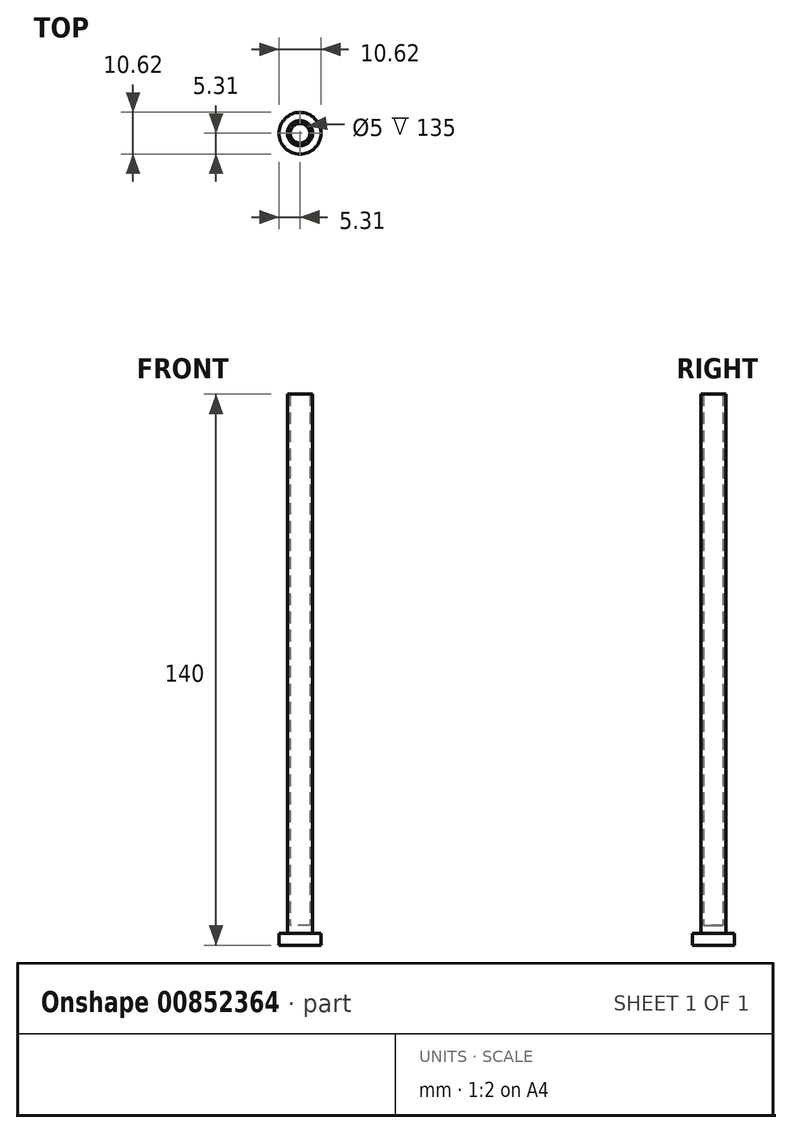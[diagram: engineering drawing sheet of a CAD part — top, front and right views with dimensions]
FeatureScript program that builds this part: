
annotation { "Feature Type Name" : "Feature", "Feature Type Description" : "" }
export const myFeature = defineFeature(function(context is Context, id is Id, definition is map)
    precondition{}
    {
        {
            var Q0;
            Q0=qCreatedBy(makeId("Top.planeOp"),FACE);
            var sketch = newSketch(context, id + "F0", { "sketchPlane" : qUnion([Q0])});
            skCircle(sketch, "E0", {"center": v(0, 0) * mm, "radius": 2.5 * mm});
            skCircle(sketch, "E1.0", {"center": v(0, 0) * mm, "radius": 3.2 * mm});
            skCircle(sketch, "E2", {"center": v(0, 0) * mm, "radius": 5.3 * mm});
            skSolve(sketch);
        }
        {
            var Q0;
            Q0 = qSketchRegion(id + "F0", true);
            var Q1;
            Q1=makeQuery(id+"F0.imprint","IMPRINT",FACE,{"disambiguationData":[TD([[makeQuery(id+"F0.imprint","IMPRINT",EDGE,{"derivedFrom":sQuery(id+"F0.wireOp",EDGE,"E0")}),-1.0]])]});
            var Q2;
            Q2=makeQuery(id+"F0.imprint","IMPRINT",FACE,{"disambiguationData":[TD([[makeQuery(id+"F0.imprint","IMPRINT",EDGE,{"derivedFrom":sQuery(id+"F0.wireOp",EDGE,"E0")}),1.0]])]});
            extrude(context, id + "F1", {"entities" : qUnion([Q0, Q1, Q2]), "depth" : 3 * mm, "offsetDistance" : 25 * mm});
        }
        {
            var Q0;
            Q0=makeQuery(id+"F0.imprint","IMPRINT",FACE,{"disambiguationData":[TD([[makeQuery(id+"F0.imprint","IMPRINT",EDGE,{"derivedFrom":sQuery(id+"F0.wireOp",EDGE,"E0")}),-1.0]])]});
            var Q1;
            Q1=makeQuery(id+"F0.imprint","IMPRINT",FACE,{"disambiguationData":[TD([[makeQuery(id+"F0.imprint","IMPRINT",EDGE,{"derivedFrom":sQuery(id+"F0.wireOp",EDGE,"E0")}),1.0]])]});
            extrude(context, id + "F2", {"entities" : qUnion([Q0, Q1]), "operationType" : NewBodyOperationType.ADD, "depth" : 5 * mm, "offsetDistance" : 25 * mm});
        }
        {
            var Q0;
            Q0=makeQuery(id+"F0.imprint","IMPRINT",FACE,{"disambiguationData":[TD([[makeQuery(id+"F0.imprint","IMPRINT",EDGE,{"derivedFrom":sQuery(id+"F0.wireOp",EDGE,"E0")}),-1.0]])]});
            extrude(context, id + "F3", {"entities" : qUnion([Q0]), "operationType" : NewBodyOperationType.ADD, "depth" : 140 * mm, "offsetDistance" : 25 * mm});
        }
    });
